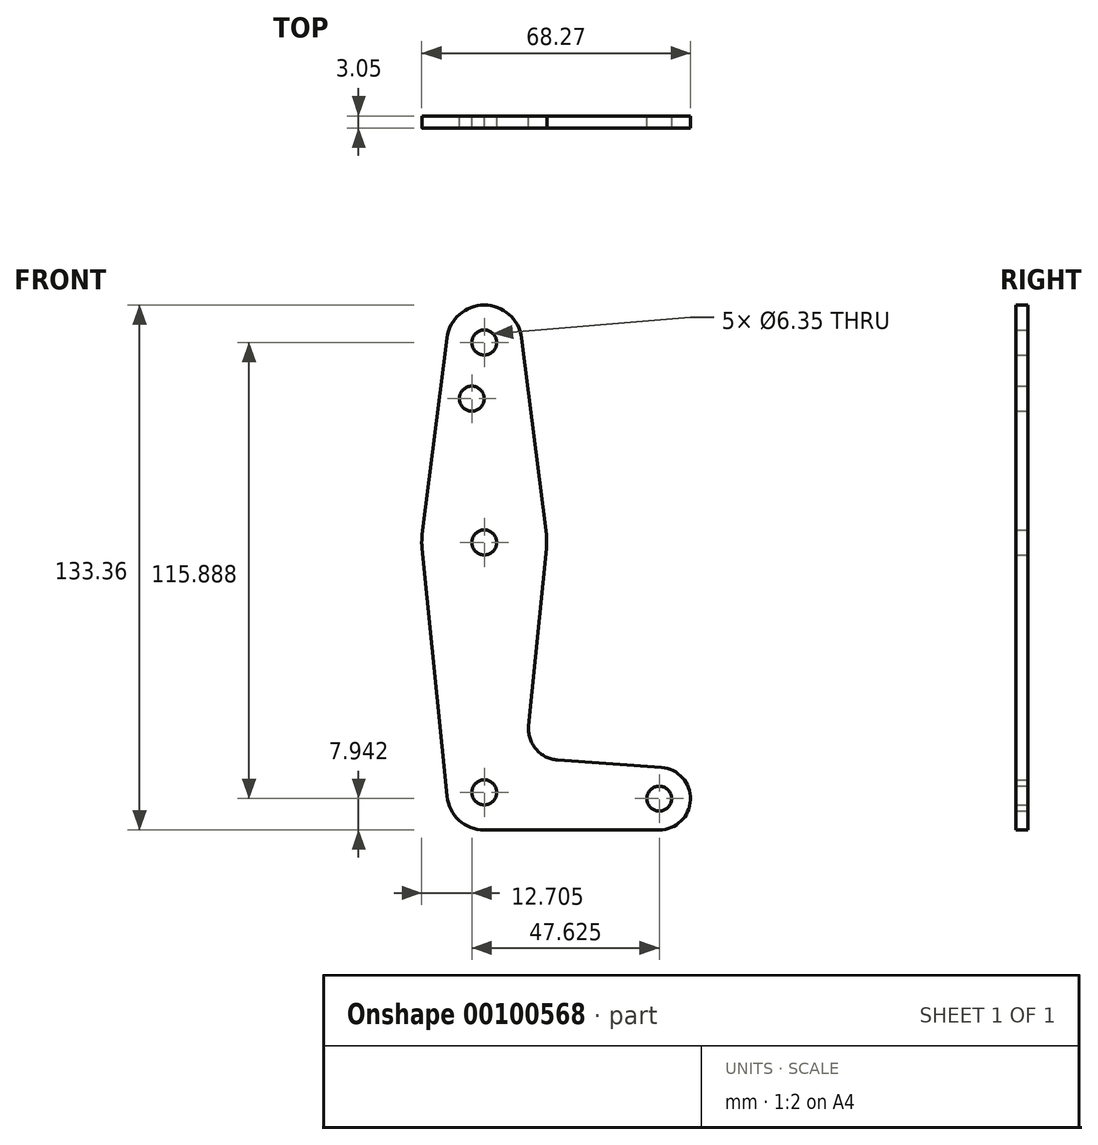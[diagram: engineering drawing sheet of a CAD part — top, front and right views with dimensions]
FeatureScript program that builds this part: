
annotation { "Feature Type Name" : "Feature", "Feature Type Description" : "" }
export const myFeature = defineFeature(function(context is Context, id is Id, definition is map)
    precondition{}
    {
        {
            var Q0;
            Q0=qCreatedBy(makeId("Front.planeOp"),FACE);
            var sketch = newSketch(context, id + "F0", { "sketchPlane" : qUnion([Q0])});
            skLineSegment(sketch, "E0", {"start": v(0, 114.3) * mm, "end": v(0, 0) * mm, "construction": true});
            skCircle(sketch, "E1", {"center": v(0, 114.3) * mm, "radius": 9.53 * mm});
            skCircle(sketch, "E2", {"center": v(0, 63.5) * mm, "radius": 15.88 * mm});
            skCircle(sketch, "E3", {"center": v(0, 0) * mm, "radius": 9.53 * mm});
            skCircle(sketch, "E4", {"center": v(44.45, -1.59) * mm, "radius": 7.94 * mm});
            skLineSegment(sketch, "E5", {"start": v(0, 0) * mm, "end": v(44.45, -1.59) * mm, "construction": true});
            skLineSegment(sketch, "E6", {"start": v(-9.45, 115.5) * mm, "end": v(-15.75, 65.48) * mm});
            skLineSegment(sketch, "E7", {"start": v(9.45, 115.5) * mm, "end": v(15.75, 65.48) * mm});
            skLineSegment(sketch, "E8", {"start": v(15.8, 61.91) * mm, "end": v(11.28, 16.94) * mm});
            skLineSegment(sketch, "E9", {"start": v(-15.8, 61.91) * mm, "end": v(-9.48, -0.95) * mm});
            skLineSegment(sketch, "E10", {"start": v(0, -9.53) * mm, "end": v(44.45, -9.52) * mm});
            skLineSegment(sketch, "E11", {"start": v(18.62, 8.22) * mm, "end": v(45.02, 6.33) * mm});
            skCircle(sketch, "E12", {"center": v(0, 114.3) * mm, "radius": 3.18 * mm});
            skCircle(sketch, "E13", {"center": v(-3.17, 100.03) * mm, "radius": 3.18 * mm});
            skCircle(sketch, "E14", {"center": v(0, 63.5) * mm, "radius": 3.18 * mm});
            skCircle(sketch, "E15", {"center": v(0, 0) * mm, "radius": 3.18 * mm});
            skCircle(sketch, "E16", {"center": v(44.45, -1.59) * mm, "radius": 3.18 * mm});
            skArc(sketch, "E17.filletArc", {"start": v(11.28, 16.94) * mm, "mid": v(13.1, 11.03) * mm, "end": v(18.62, 8.22) * mm});
            skSolve(sketch);
        }
        {
            var Q0;
            Q0=makeQuery(id+"F0.imprint","IMPRINT",FACE,{"disambiguationData":[TD([[makeQuery(id+"F0.imprint","IMPRINT",EDGE,{"derivedFrom":sQuery(id+"F0.wireOp",EDGE,"E12")}),-1.0]])]});
            var Q1;
            {var subQ1=sQuery(id+"F0.wireOp",EDGE,"E6");Q1=makeQuery(id+"F0.imprint","IMPRINT",FACE,{"disambiguationData":[TD([[makeQuery(id+"F0.imprint","IMPRINT",EDGE,{"derivedFrom":subQ1}),1.0]])]});}
            var Q2;
            Q2=makeQuery(id+"F0.imprint","IMPRINT",FACE,{"disambiguationData":[TD([[makeQuery(id+"F0.imprint","IMPRINT",EDGE,{"derivedFrom":sQuery(id+"F0.wireOp",EDGE,"E14")}),-1.0]])]});
            var Q3;
            {var subQ0=sQuery(id+"F0.wireOp",EDGE,"E8");Q3=makeQuery(id+"F0.imprint","IMPRINT",FACE,{"disambiguationData":[TD([[makeQuery(id+"F0.imprint","IMPRINT",EDGE,{"derivedFrom":subQ0}),-1.0]])]});}
            var Q4;
            Q4=makeQuery(id+"F0.imprint","IMPRINT",FACE,{"disambiguationData":[TD([[makeQuery(id+"F0.imprint","IMPRINT",EDGE,{"derivedFrom":sQuery(id+"F0.wireOp",EDGE,"E16")}),-1.0]])]});
            var Q5;
            Q5=makeQuery(id+"F0.imprint","IMPRINT",FACE,{"disambiguationData":[TD([[makeQuery(id+"F0.imprint","IMPRINT",EDGE,{"derivedFrom":sQuery(id+"F0.wireOp",EDGE,"E15")}),-1.0]])]});
            extrude(context, id + "F1", {"entities" : qUnion([Q0, Q1, Q2, Q3, Q4, Q5]), "depth" : 3.05 * mm});
        }
    });
